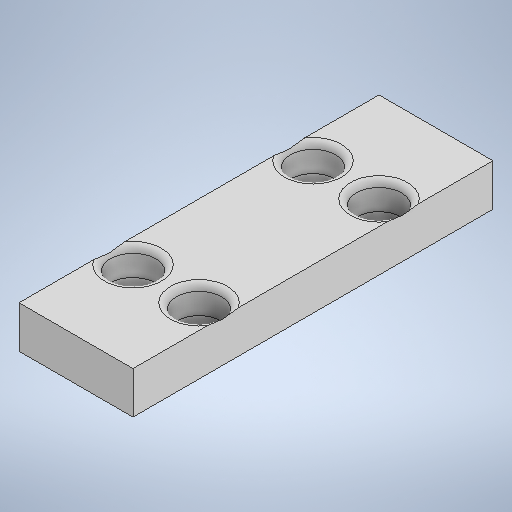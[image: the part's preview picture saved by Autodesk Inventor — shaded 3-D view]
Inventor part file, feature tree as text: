
AUTODESK INVENTOR PART (.ipt)
format: ipt  version: 2025.1 (Build 291241000, 241)  size: 343,552 bytes
history: native  units: mm
features: extrude x2, sketch x2, fillet x1
ambient origin geometry x8: Origin, YZ Plane, XZ Plane, XY Plane, X Axis, Y Axis, Z Axis, Center Point
bodies: Solide1 (feature_tree)
feature tree (5):
  extrude  "Extrusion1"  Depth=19.0mm
  extrude  "Extrusion2"  Depth=60.0mm
  fillet  "Congé2"  Radius=15.0mm
  sketch  "Esquisse1"
  sketch  "Esquisse2"
